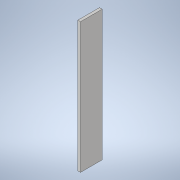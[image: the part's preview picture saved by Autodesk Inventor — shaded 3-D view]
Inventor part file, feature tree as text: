
AUTODESK INVENTOR PART (.ipt)
format: ipt  version: 2020 (Build 240168000, 168)  size: 92,160 bytes
history: native  units: mm
features: sketch x1, extrude x1
ambient origin geometry x8: Origin, YZ Plane, XZ Plane, XY Plane, X Axis, Y Axis, Z Axis, Center Point
bodies: Solid1 (feature_tree)
feature tree (2):
  sketch  "Sketch2"  dims[d0=241.0mm d1=40.0mm d2=5.0mm d3=0.0mm]
  extrude  "Extrusion1"  Depth=40.0mm
